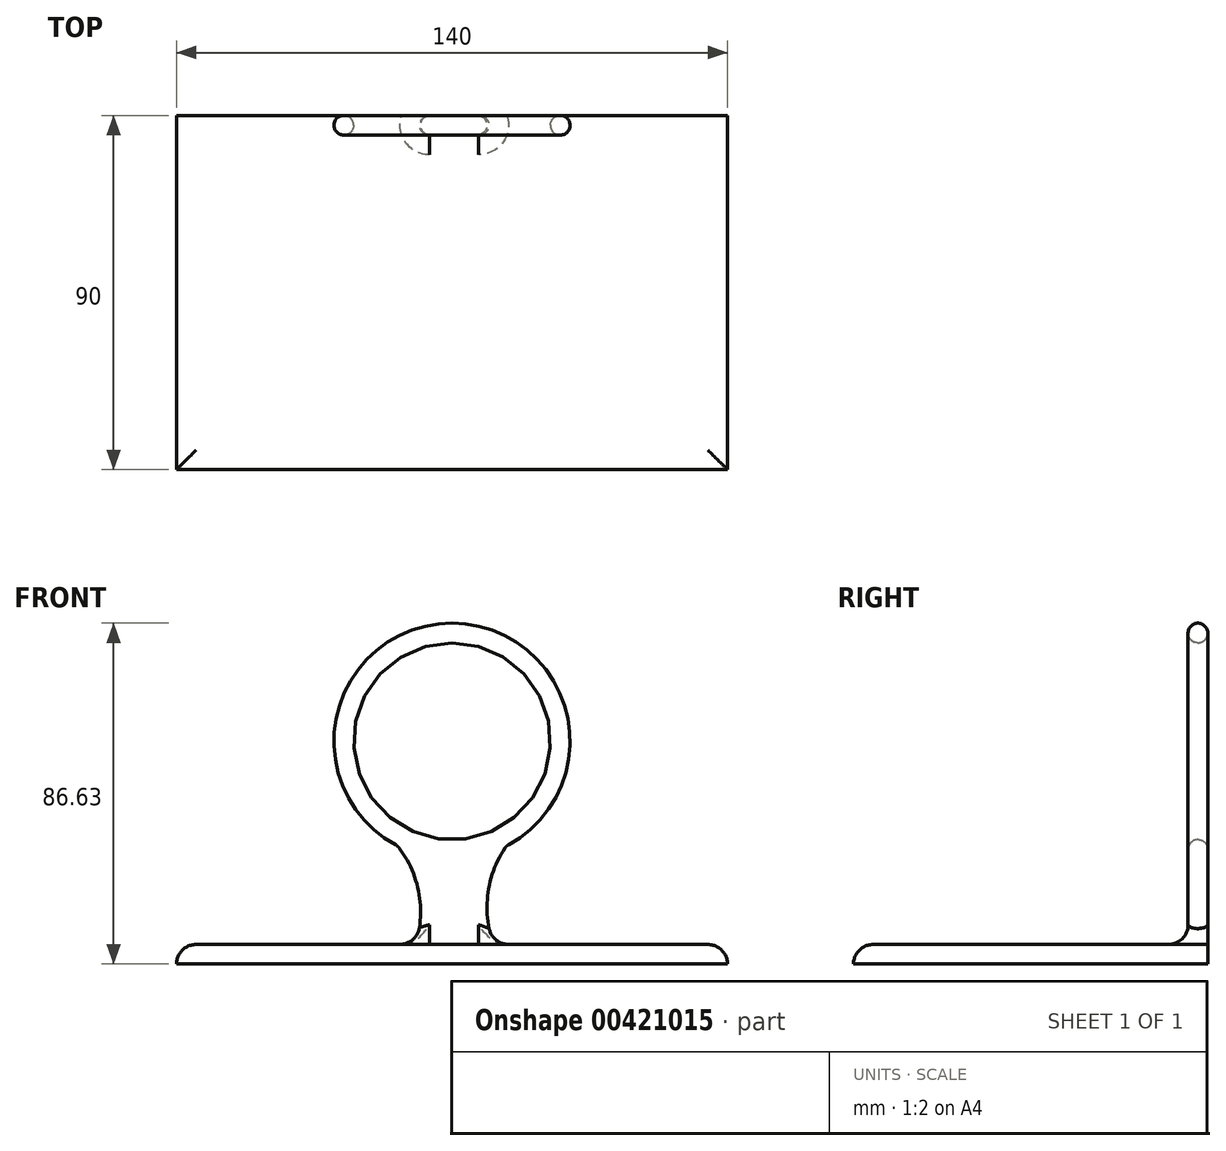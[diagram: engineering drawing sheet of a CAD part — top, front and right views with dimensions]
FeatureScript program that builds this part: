
annotation { "Feature Type Name" : "Feature", "Feature Type Description" : "" }
export const myFeature = defineFeature(function(context is Context, id is Id, definition is map)
    precondition{}
    {
        {
            var Q0;
            Q0=qCreatedBy(makeId("Front.planeOp"),FACE);
            var sketch = newSketch(context, id + "F0", { "sketchPlane" : qUnion([Q0])});
            skArc(sketch, "E0", {"start": v(13.81, -26.63) * mm, "mid": v(0, 30) * mm, "end": v(-13.81, -26.63) * mm});
            skCircle(sketch, "E1.0", {"center": v(0, 0) * mm, "radius": 25 * mm});
            skArc(sketch, "E2", {"start": v(-11.44, -56.63) * mm, "mid": v(-8.06, -41.27) * mm, "end": v(-13.81, -26.63) * mm});
            skArc(sketch, "E3", {"start": v(13.81, -26.63) * mm, "mid": v(8.9, -41.52) * mm, "end": v(13.1, -56.63) * mm});
            skLineSegment(sketch, "E4", {"start": v(-11.44, -56.63) * mm, "end": v(13.1, -56.63) * mm});
            skSolve(sketch);
        }
        {
            var Q0;
            Q0 = qSketchRegion(id + "F0", true);
            extrude(context, id + "F1", {"entities" : qUnion([Q0]), "depth" : 5 * mm});
        }
        {
            var Q0;
            Q0=makeQuery(id+"F1.opExtrude","CAP_EDGE",EDGE,{"disambiguationData":[OSD([sQuery(id+"F0.wireOp",EDGE,"E0")])],"isStart":false});
            var Q1;
            Q1=makeQuery(id+"F1.opExtrude","CAP_EDGE",EDGE,{"disambiguationData":[OSD([sQuery(id+"F0.wireOp",EDGE,"E1.0")])],"isStart":false});
            var Q2;
            Q2=makeQuery(id+"F1.opExtrude","CAP_EDGE",EDGE,{"disambiguationData":[OSD([sQuery(id+"F0.wireOp",EDGE,"E0")])],"isStart":true});
            var Q3;
            Q3=makeQuery(id+"F1.opExtrude","CAP_EDGE",EDGE,{"disambiguationData":[OSD([sQuery(id+"F0.wireOp",EDGE,"E1.0")])],"isStart":true});
            var Q4;
            Q4=makeQuery(id+"F1.opExtrude","CAP_EDGE",EDGE,{"disambiguationData":[OSD([sQuery(id+"F0.wireOp",EDGE,"E3")])],"isStart":false});
            var Q5;
            Q5=makeQuery(id+"F1.opExtrude","CAP_FACE",FACE,{"disambiguationData":[OSD([sQuery(id+"F0.wireOp",EDGE,"E0"),sQuery(id+"F0.wireOp",EDGE,"E1.0"),sQuery(id+"F0.wireOp",EDGE,"E2"),sQuery(id+"F0.wireOp",EDGE,"E3"),sQuery(id+"F0.wireOp",EDGE,"E4")])],"isStart":false});
            var Q6;
            Q6=makeQuery(id+"F1.opExtrude","CAP_EDGE",EDGE,{"disambiguationData":[OSD([sQuery(id+"F0.wireOp",EDGE,"E2")])],"isStart":true});
            var Q7;
            Q7=makeQuery(id+"F1.opExtrude","CAP_EDGE",EDGE,{"disambiguationData":[OSD([sQuery(id+"F0.wireOp",EDGE,"E3")])],"isStart":true});
            var Q8;
            Q8=makeQuery(id+"F1.opExtrude","SWEPT_EDGE",EDGE,{"disambiguationData":[OSD([sQuery(id+"F0.wireOp",EDGE,"E0"),sQuery(id+"F0.wireOp",EDGE,"E2")])]});
            var Q9;
            Q9=makeQuery(id+"F1.opExtrude","SWEPT_EDGE",EDGE,{"disambiguationData":[OSD([sQuery(id+"F0.wireOp",EDGE,"E0"),sQuery(id+"F0.wireOp",EDGE,"E3")])]});
            fillet(context, id + "F2", {"entities" : qUnion([Q0, Q1, Q2, Q3, Q4, Q5, Q6, Q7, Q8, Q9]), "radius" : 2.5 * mm, "tangentPropagation" : true, "allowEdgeOverflow" : false});
        }
        {
            var Q0;
            {var subQ0=sQuery(id+"F0.wireOp",EDGE,"E4");Q0=makeQuery(id+"F2.opFillet","BLEND_EDGE",EDGE,{"blendedFrom":[makeQuery(id+"F1.opExtrude","CAP_EDGE",EDGE,{"disambiguationData":[OSD([subQ0])],"isStart":false}),makeQuery(id+"F1.opExtrude","SWEPT_FACE",FACE,{"disambiguationData":[OSD([subQ0])]})],"blendedInto":[makeQuery(id+"F1.opExtrude","SWEPT_FACE",FACE,{"disambiguationData":[OSD([subQ0])]})]});}
            cPlane(context, id + "F3", {"entities" : qUnion([Q0]), "cplaneType" : CPlaneType.LINE_ANGLE, "offset" : 25 * mm, "angle" : 90 * degree, "width" : 150 * mm, "height" : 150 * mm});
        }
        {
            var Q0;
            Q0=qCreatedBy(id+"F3.planeOp",FACE);
            var sketch = newSketch(context, id + "F4", { "sketchPlane" : qUnion([Q0])});
            skLineSegment(sketch, "E5", {"start": v(0, 0) * mm, "end": v(70, 0) * mm});
            skLineSegment(sketch, "E6", {"start": v(0, 0) * mm, "end": v(-70, 0) * mm});
            skLineSegment(sketch, "E7", {"start": v(-70, 0) * mm, "end": v(-70, -0.64) * mm});
            skLineSegment(sketch, "E8", {"start": v(-70, 0) * mm, "end": v(-70, -90) * mm});
            skLineSegment(sketch, "E9", {"start": v(70, 0) * mm, "end": v(70, -90) * mm});
            skLineSegment(sketch, "E10", {"start": v(-70, -90) * mm, "end": v(70, -90) * mm});
            skSolve(sketch);
        }
        {
            var Q0;
            Q0 = qSketchRegion(id + "F4", true);
            extrude(context, id + "F5", {"entities" : qUnion([Q0]), "operationType" : NewBodyOperationType.ADD, "depth" : 5 * mm});
        }
        {
            var Q0;
            Q0=makeQuery(id+"F5.opExtrude","CAP_EDGE",EDGE,{"disambiguationData":[OSD([sQuery(id+"F4.wireOp",EDGE,"E10")])],"isStart":false});
            var Q1;
            Q1=makeQuery(id+"F5.opExtrude","CAP_EDGE",EDGE,{"disambiguationData":[OSD([sQuery(id+"F4.wireOp",EDGE,"E9")])],"isStart":false});
            var Q2;
            Q2=makeQuery(id+"F5.opExtrude","CAP_EDGE",EDGE,{"disambiguationData":[OSD([sQuery(id+"F4.wireOp",EDGE,"E8")])],"isStart":false});
            var Q3;
            Q3=makeQuery(id+"F2.opFillet","BLEND_FACE",FACE,{"disambiguationData":[OSD([sQuery(id+"F0.wireOp",EDGE,"E2")])]});
            fillet(context, id + "F6", {"entities" : qUnion([Q0, Q1, Q2, Q3]), "radius" : 5 * mm, "tangentPropagation" : true, "allowEdgeOverflow" : false});
        }
    });
